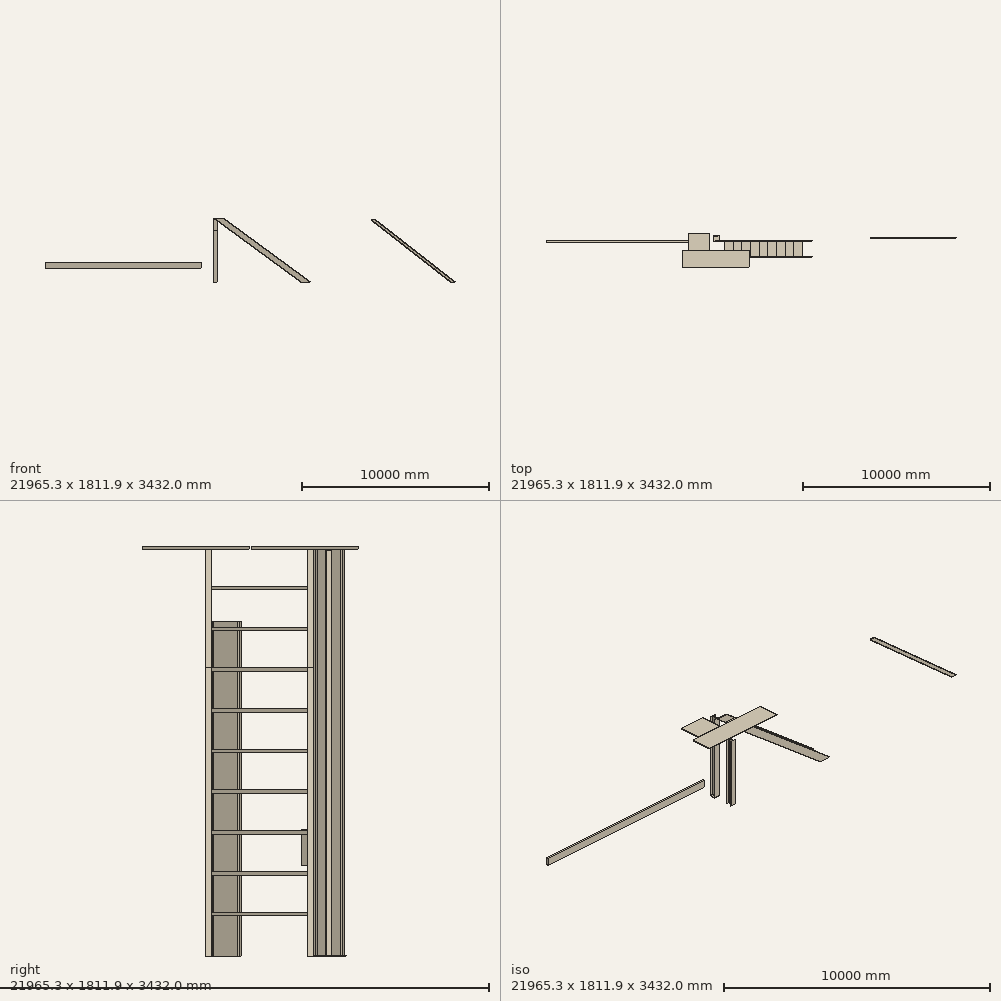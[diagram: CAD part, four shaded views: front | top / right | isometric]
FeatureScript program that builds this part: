
annotation { "Feature Type Name" : "Feature", "Feature Type Description" : "" }
export const myFeature = defineFeature(function(context is Context, id is Id, definition is map)
    precondition{}
    {
        {
            var Q0;
            Q0=qCreatedBy(makeId("Top.planeOp"),FACE);
            var sketch = newSketch(context, id + "F0", { "sketchPlane" : qUnion([Q0])});
            skLineSegment(sketch, "E0.bottom", {"start": v(120, 150) * mm, "end": v(-120, 150) * mm});
            skLineSegment(sketch, "E0.top", {"start": v(120, -150) * mm, "end": v(-120, -150) * mm});
            skLineSegment(sketch, "E0.left", {"start": v(150, 120) * mm, "end": v(150, -120) * mm});
            skLineSegment(sketch, "E0.right", {"start": v(-150, 120) * mm, "end": v(-150, -120) * mm});
            skPoint(sketch, "E0.middle", {"position": v(0, 0) * mm});
            skPoint(sketch, "E1.visualSharp", {"position": v(-150, 150) * mm});
            skArc(sketch, "E1.filletArc", {"start": v(-120, 150) * mm, "mid": v(-141.21, 141.21) * mm, "end": v(-150, 120) * mm});
            skPoint(sketch, "E2.visualSharp", {"position": v(150, 150) * mm});
            skArc(sketch, "E2.filletArc", {"start": v(150, 120) * mm, "mid": v(141.21, 141.21) * mm, "end": v(120, 150) * mm});
            skPoint(sketch, "E3.visualSharp", {"position": v(150, -150) * mm});
            skArc(sketch, "E3.filletArc", {"start": v(120, -150) * mm, "mid": v(141.21, -141.21) * mm, "end": v(150, -120) * mm});
            skPoint(sketch, "E4.visualSharp", {"position": v(-150, -150) * mm});
            skArc(sketch, "E4.filletArc", {"start": v(-150, -120) * mm, "mid": v(-141.21, -141.21) * mm, "end": v(-120, -150) * mm});
            skSolve(sketch);
        }
        {
            var Q0;
            Q0=makeQuery(id+"F0.imprint","IMPRINT",FACE,{"disambiguationData":[TD([[makeQuery(id+"F0.imprint","IMPRINT",EDGE,{"derivedFrom":sQuery(id+"F0.wireOp",EDGE,"E0.bottom")}),1.0]])]});
            extrude(context, id + "F1", {"entities" : qUnion([Q0]), "depth" : 10 * mm, "offsetDistance" : 25 * mm});
        }
        {
            var Q0;
            Q0=makeQuery(id+"F1.opExtrude","CAP_FACE",FACE,{"disambiguationData":[OSD([sQuery(id+"F0.wireOp",EDGE,"E0.bottom"),sQuery(id+"F0.wireOp",EDGE,"E0.top"),sQuery(id+"F0.wireOp",EDGE,"E0.left"),sQuery(id+"F0.wireOp",EDGE,"E0.right"),sQuery(id+"F0.wireOp",EDGE,"E1.filletArc"),sQuery(id+"F0.wireOp",EDGE,"E2.filletArc"),sQuery(id+"F0.wireOp",EDGE,"E3.filletArc"),sQuery(id+"F0.wireOp",EDGE,"E4.filletArc")])],"isStart":false});
            var sketch = newSketch(context, id + "F2", { "sketchPlane" : qUnion([Q0])});
            skLineSegment(sketch, "E5", {"start": v(-128, 130) * mm, "end": v(128, 130) * mm});
            skLineSegment(sketch, "E6", {"start": v(128, 130) * mm, "end": v(128, 112.7) * mm});
            skLineSegment(sketch, "E7", {"start": v(128, 112.7) * mm, "end": v(19.25, 112.7) * mm});
            skArc(sketch, "E8", {"start": v(19.25, 112.7) * mm, "mid": v(9.35, 108.6) * mm, "end": v(5.25, 98.7) * mm});
            skLineSegment(sketch, "E9", {"start": v(5.25, 98.7) * mm, "end": v(5.25, -98.7) * mm});
            skArc(sketch, "E10", {"start": v(5.25, -98.7) * mm, "mid": v(9.35, -108.6) * mm, "end": v(19.25, -112.7) * mm});
            skLineSegment(sketch, "E11", {"start": v(19.25, -112.7) * mm, "end": v(128, -112.7) * mm});
            skLineSegment(sketch, "E12", {"start": v(128, -112.7) * mm, "end": v(128, -130) * mm});
            skLineSegment(sketch, "E13", {"start": v(-128, -130) * mm, "end": v(-128, -112.7) * mm});
            skLineSegment(sketch, "E14", {"start": v(-128, -112.7) * mm, "end": v(-19.25, -112.7) * mm});
            skArc(sketch, "E15", {"start": v(-19.25, -112.7) * mm, "mid": v(-9.35, -108.6) * mm, "end": v(-5.25, -98.7) * mm});
            skLineSegment(sketch, "E16", {"start": v(-5.25, -98.7) * mm, "end": v(-5.25, 98.7) * mm});
            skArc(sketch, "E17", {"start": v(-5.25, 98.7) * mm, "mid": v(-9.35, 108.6) * mm, "end": v(-19.25, 112.7) * mm});
            skLineSegment(sketch, "E18", {"start": v(-19.25, 112.7) * mm, "end": v(-128, 112.7) * mm});
            skLineSegment(sketch, "E19", {"start": v(-128, 112.7) * mm, "end": v(-128, 130) * mm});
            skLineSegment(sketch, "E20", {"start": v(-128, -130) * mm, "end": v(128, -130) * mm});
            skLineSegment(sketch, "E21", {"start": v(5.25, 0) * mm, "end": v(-5.25, 0) * mm});
            skPoint(sketch, "E22", {"position": v(0, 0) * mm});
            skSolve(sketch);
        }
        {
            var Q0;
            Q0=qSketchRegion(id+"F2",true);
            extrude(context, id + "F3", {"entities" : qUnion([Q0]), "operationType" : NewBodyOperationType.ADD, "depth" : 3400 * mm, "offsetDistance" : 25 * mm});
        }
        {
            var Q0;
            Q0=makeQuery(id+"F1.opExtrude","CAP_FACE",FACE,{"disambiguationData":[OSD([sQuery(id+"F0.wireOp",EDGE,"E0.bottom"),sQuery(id+"F0.wireOp",EDGE,"E0.top"),sQuery(id+"F0.wireOp",EDGE,"E0.left"),sQuery(id+"F0.wireOp",EDGE,"E0.right"),sQuery(id+"F0.wireOp",EDGE,"E1.filletArc"),sQuery(id+"F0.wireOp",EDGE,"E2.filletArc"),sQuery(id+"F0.wireOp",EDGE,"E3.filletArc"),sQuery(id+"F0.wireOp",EDGE,"E4.filletArc")])],"isStart":false});
            var sketch = newSketch(context, id + "F4", { "sketchPlane" : qUnion([Q0])});
            skLineSegment(sketch, "E23", {"start": v(125, -75) * mm, "end": v(125, 75) * mm, "construction": true});
            skLineSegment(sketch, "E24", {"start": v(0, 150) * mm, "end": v(0, -150) * mm, "construction": true});
            skCircle(sketch, "E25", {"center": v(125, -75) * mm, "radius": 12.5 * mm});
            skCircle(sketch, "E26", {"center": v(125, 75) * mm, "radius": 12.5 * mm});
            skLineSegment(sketch, "E27", {"start": v(125, 0) * mm, "end": v(150, 0) * mm, "construction": true});
            skCircle(sketch, "E28.MirrorC", {"center": v(-125, -75) * mm, "radius": 12.5 * mm});
            skCircle(sketch, "E29.MirrorC", {"center": v(-125, 75) * mm, "radius": 12.5 * mm});
            skSolve(sketch);
        }
        {
            var Q0;
            Q0=qSketchRegion(id+"F4",true);
            extrude(context, id + "F5", {"entities" : qUnion([Q0]), "operationType" : NewBodyOperationType.REMOVE, "oppositeDirection" : true, "depth" : 25 * mm, "offsetDistance" : 25 * mm});
        }
        {
            var Q0;
            Q0=qCreatedBy(makeId("Top.planeOp"),FACE);
            cPlane(context, id + "F6", {"entities" : qUnion([Q0]), "cplaneType" : CPlaneType.OFFSET, "offset" : 1210 * mm, "width" : 150 * mm, "height" : 150 * mm});
        }
        {
            var Q0;
            Q0=makeQuery(id+"F3.opExtrude","SWEPT_FACE",FACE,{"disambiguationData":[OSD([sQuery(id+"F2.wireOp",EDGE,"E20")])]});
            var sketch = newSketch(context, id + "F7", { "sketchPlane" : qUnion([Q0])});
            skLineSegment(sketch, "E30.bottom", {"start": v(-9105.2, 1063.83) * mm, "end": v(-775.2, 1063.83) * mm});
            skLineSegment(sketch, "E30.top", {"start": v(-9105.2, 763.83) * mm, "end": v(-775.2, 763.83) * mm});
            skLineSegment(sketch, "E30.left", {"start": v(-9105.2, 1063.83) * mm, "end": v(-9105.2, 763.83) * mm});
            skLineSegment(sketch, "E30.right", {"start": v(-775.2, 1063.83) * mm, "end": v(-775.2, 763.83) * mm});
            skSolve(sketch);
        }
        {
            var Q0;
            Q0 = qSketchRegion(id + "F7", true);
            extrude(context, id + "F8", {"entities" : qUnion([Q0]), "depth" : 100 * mm, "offsetDistance" : 25 * mm});
        }
        {
            var Q0;
            Q0=qCreatedBy(makeId("Top.planeOp"),FACE);
            var sketch = newSketch(context, id + "F9", { "sketchPlane" : qUnion([Q0])});
            skLineSegment(sketch, "E31", {"start": v(-128, -733) * mm, "end": v(128, -733) * mm});
            skLineSegment(sketch, "E32", {"start": v(128, -733) * mm, "end": v(128, -750.3) * mm});
            skLineSegment(sketch, "E33", {"start": v(128, -750.3) * mm, "end": v(19.25, -750.3) * mm});
            skArc(sketch, "E34", {"start": v(19.25, -750.3) * mm, "mid": v(9.35, -754.4) * mm, "end": v(5.25, -764.3) * mm});
            skLineSegment(sketch, "E35", {"start": v(5.25, -764.3) * mm, "end": v(5.25, -961.7) * mm});
            skArc(sketch, "E36", {"start": v(5.25, -961.7) * mm, "mid": v(9.35, -971.6) * mm, "end": v(19.25, -975.7) * mm});
            skLineSegment(sketch, "E37", {"start": v(19.25, -975.7) * mm, "end": v(128, -975.7) * mm});
            skLineSegment(sketch, "E38", {"start": v(128, -975.7) * mm, "end": v(128, -993) * mm});
            skLineSegment(sketch, "E39", {"start": v(-128, -993) * mm, "end": v(-128, -975.7) * mm});
            skLineSegment(sketch, "E40", {"start": v(-128, -975.7) * mm, "end": v(-19.25, -975.7) * mm});
            skArc(sketch, "E41", {"start": v(-19.25, -975.7) * mm, "mid": v(-9.35, -971.6) * mm, "end": v(-5.25, -961.7) * mm});
            skLineSegment(sketch, "E42", {"start": v(-5.25, -961.7) * mm, "end": v(-5.25, -764.3) * mm});
            skArc(sketch, "E43", {"start": v(-5.25, -764.3) * mm, "mid": v(-9.35, -754.4) * mm, "end": v(-19.25, -750.3) * mm});
            skLineSegment(sketch, "E44", {"start": v(-19.25, -750.3) * mm, "end": v(-128, -750.3) * mm});
            skLineSegment(sketch, "E45", {"start": v(-128, -750.3) * mm, "end": v(-128, -733) * mm});
            skLineSegment(sketch, "E46", {"start": v(-128, -993) * mm, "end": v(128, -993) * mm});
            skLineSegment(sketch, "E47", {"start": v(5.25, -863) * mm, "end": v(-5.25, -863) * mm});
            skPoint(sketch, "E48", {"position": v(0, -863) * mm});
            skSolve(sketch);
        }
        {
            var Q0;
            Q0 = qSketchRegion(id + "F9", true);
            extrude(context, id + "F10", {"entities" : qUnion([Q0]), "depth" : 2800 * mm, "offsetDistance" : 25 * mm});
        }
        {
            var Q0;
            Q0=makeQuery(id+"F3.opExtrude","CAP_FACE",FACE,{"disambiguationData":[OSD([sQuery(id+"F2.wireOp",EDGE,"E5"),sQuery(id+"F2.wireOp",EDGE,"E6"),sQuery(id+"F2.wireOp",EDGE,"E7"),sQuery(id+"F2.wireOp",EDGE,"E8"),sQuery(id+"F2.wireOp",EDGE,"E9"),sQuery(id+"F2.wireOp",EDGE,"E10"),sQuery(id+"F2.wireOp",EDGE,"E11"),sQuery(id+"F2.wireOp",EDGE,"E12"),sQuery(id+"F2.wireOp",EDGE,"E13"),sQuery(id+"F2.wireOp",EDGE,"E14"),sQuery(id+"F2.wireOp",EDGE,"E15"),sQuery(id+"F2.wireOp",EDGE,"E16"),sQuery(id+"F2.wireOp",EDGE,"E17"),sQuery(id+"F2.wireOp",EDGE,"E18"),sQuery(id+"F2.wireOp",EDGE,"E19"),sQuery(id+"F2.wireOp",EDGE,"E20")])],"isStart":false});
            var sketch = newSketch(context, id + "F11", { "sketchPlane" : qUnion([Q0])});
            skLineSegment(sketch, "E49.bottom", {"start": v(-1838.16, -1561.65) * mm, "end": v(1761.84, -1561.65) * mm});
            skLineSegment(sketch, "E49.top", {"start": v(-1838.16, -661.65) * mm, "end": v(1761.84, -661.65) * mm});
            skLineSegment(sketch, "E49.left", {"start": v(-1838.16, -1561.65) * mm, "end": v(-1838.16, -661.65) * mm});
            skLineSegment(sketch, "E49.right", {"start": v(1761.84, -1561.65) * mm, "end": v(1761.84, -661.65) * mm});
            skSolve(sketch);
        }
        {
            var Q0;
            Q0=makeQuery(id+"F11.imprint","IMPRINT",FACE,{"disambiguationData":[TD([[makeQuery(id+"F11.imprint","IMPRINT",EDGE,{"derivedFrom":sQuery(id+"F11.wireOp",EDGE,"E49.bottom")}),1.0]])]});
            extrude(context, id + "F12", {"entities" : qUnion([Q0]), "depth" : 22 * mm, "offsetDistance" : 25 * mm});
        }
        {
            var Q0;
            Q0=makeQuery(id+"F12.opExtrude","CAP_FACE",FACE,{"disambiguationData":[OSD([sQuery(id+"F11.wireOp",EDGE,"E49.bottom"),sQuery(id+"F11.wireOp",EDGE,"E49.top"),sQuery(id+"F11.wireOp",EDGE,"E49.left"),sQuery(id+"F11.wireOp",EDGE,"E49.right")])],"isStart":false});
            var sketch = newSketch(context, id + "F13", { "sketchPlane" : qUnion([Q0])});
            skLineSegment(sketch, "E50.bottom", {"start": v(-1505.54, 250.28) * mm, "end": v(-375.54, 250.28) * mm});
            skLineSegment(sketch, "E50.top", {"start": v(-1505.54, -649.72) * mm, "end": v(-375.54, -649.72) * mm});
            skLineSegment(sketch, "E50.left", {"start": v(-1505.54, 250.28) * mm, "end": v(-1505.54, -649.72) * mm});
            skLineSegment(sketch, "E50.right", {"start": v(-375.54, 250.28) * mm, "end": v(-375.54, -649.72) * mm});
            skSolve(sketch);
        }
        {
            var Q0;
            Q0=makeQuery(id+"F13.imprint","IMPRINT",FACE,{"disambiguationData":[TD([[makeQuery(id+"F13.imprint","IMPRINT",EDGE,{"derivedFrom":sQuery(id+"F13.wireOp",EDGE,"E50.bottom")}),-1.0]])]});
            extrude(context, id + "F14", {"entities" : qUnion([Q0]), "oppositeDirection" : true, "depth" : 22 * mm, "offsetDistance" : 25 * mm});
        }
        {
            var Q0;
            Q0=makeQuery(id+"F3.opExtrude","SWEPT_FACE",FACE,{"disambiguationData":[OSD([sQuery(id+"F2.wireOp",EDGE,"E20")])]});
            var sketch = newSketch(context, id + "F15", { "sketchPlane" : qUnion([Q0])});
            skLineSegment(sketch, "E51.left", {"start": v(4613.26, 0) * mm, "end": v(4613.26, 341) * mm, "construction": true});
            skLineSegment(sketch, "E52.bottom", {"start": v(4613.26, 341) * mm, "end": v(4148.47, 341) * mm});
            skLineSegment(sketch, "E53.left", {"start": v(4148.47, 341) * mm, "end": v(4148.47, 682) * mm, "construction": true});
            skLineSegment(sketch, "E54.bottom", {"start": v(4148.47, 682) * mm, "end": v(3683.68, 682) * mm});
            skLineSegment(sketch, "E54.left", {"start": v(4148.47, 371) * mm, "end": v(4148.47, 341) * mm, "construction": true});
            skLineSegment(sketch, "E55", {"start": v(3683.68, 682) * mm, "end": v(3683.68, 1023) * mm, "construction": true});
            skLineSegment(sketch, "E56", {"start": v(3683.68, 1023) * mm, "end": v(3218.9, 1023) * mm});
            skLineSegment(sketch, "E57", {"start": v(3218.9, 1023) * mm, "end": v(3218.9, 1364) * mm, "construction": true});
            skLineSegment(sketch, "E58", {"start": v(3218.9, 1364) * mm, "end": v(2754.11, 1364) * mm});
            skLineSegment(sketch, "E59", {"start": v(2754.11, 1364) * mm, "end": v(2754.11, 1705) * mm, "construction": true});
            skLineSegment(sketch, "E60", {"start": v(2754.11, 1705) * mm, "end": v(2289.33, 1705) * mm});
            skLineSegment(sketch, "E61", {"start": v(2289.33, 1705) * mm, "end": v(2289.33, 2046) * mm, "construction": true});
            skLineSegment(sketch, "E62", {"start": v(2289.33, 2046) * mm, "end": v(1824.54, 2046) * mm});
            skLineSegment(sketch, "E63", {"start": v(1824.54, 2046) * mm, "end": v(1824.54, 2387) * mm, "construction": true});
            skLineSegment(sketch, "E64", {"start": v(1824.54, 2387) * mm, "end": v(1359.76, 2387) * mm});
            skLineSegment(sketch, "E65", {"start": v(1359.76, 2387) * mm, "end": v(1359.76, 2728) * mm, "construction": true});
            skLineSegment(sketch, "E66", {"start": v(1359.76, 2728) * mm, "end": v(894.97, 2728) * mm});
            skLineSegment(sketch, "E67", {"start": v(894.97, 2728) * mm, "end": v(894.97, 3069) * mm, "construction": true});
            skLineSegment(sketch, "E68", {"start": v(894.97, 3069) * mm, "end": v(430.18, 3069) * mm});
            skLineSegment(sketch, "E69", {"start": v(430.18, 3069) * mm, "end": v(430.18, 3410) * mm, "construction": true});
            skLineSegment(sketch, "E70", {"start": v(3683.68, 682) * mm, "end": v(3683.68, 652) * mm, "construction": true});
            skLineSegment(sketch, "E71", {"start": v(3683.68, 652) * mm, "end": v(4148.47, 652) * mm, "construction": true});
            skLineSegment(sketch, "E72", {"start": v(3218.9, 1023) * mm, "end": v(3218.9, 993) * mm, "construction": true});
            skLineSegment(sketch, "E73", {"start": v(3218.9, 993) * mm, "end": v(3683.68, 993) * mm, "construction": true});
            skLineSegment(sketch, "E74", {"start": v(2754.11, 1364) * mm, "end": v(2754.11, 1334) * mm, "construction": true});
            skLineSegment(sketch, "E75", {"start": v(2754.11, 1334) * mm, "end": v(3218.9, 1334) * mm, "construction": true});
            skLineSegment(sketch, "E76", {"start": v(2289.33, 1705) * mm, "end": v(2289.33, 1675) * mm, "construction": true});
            skLineSegment(sketch, "E77", {"start": v(2289.33, 1675) * mm, "end": v(2754.11, 1675) * mm, "construction": true});
            skLineSegment(sketch, "E78", {"start": v(1824.54, 2046) * mm, "end": v(1824.54, 2016) * mm, "construction": true});
            skLineSegment(sketch, "E79", {"start": v(1824.54, 2016) * mm, "end": v(2289.33, 2016) * mm, "construction": true});
            skLineSegment(sketch, "E80", {"start": v(1359.76, 2387) * mm, "end": v(1359.76, 2357) * mm, "construction": true});
            skLineSegment(sketch, "E81", {"start": v(1359.76, 2357) * mm, "end": v(1824.54, 2357) * mm, "construction": true});
            skLineSegment(sketch, "E82", {"start": v(894.97, 2728) * mm, "end": v(894.97, 2698) * mm, "construction": true});
            skLineSegment(sketch, "E83", {"start": v(894.97, 2698) * mm, "end": v(1359.76, 2698) * mm, "construction": true});
            skLineSegment(sketch, "E84", {"start": v(430.18, 3069) * mm, "end": v(430.18, 3039) * mm, "construction": true});
            skLineSegment(sketch, "E85", {"start": v(430.18, 3039) * mm, "end": v(894.97, 3039) * mm, "construction": true});
            skLineSegment(sketch, "E86", {"start": v(3683.68, 1023) * mm, "end": v(3683.68, 993) * mm, "construction": true});
            skLineSegment(sketch, "E87", {"start": v(3218.9, 1364) * mm, "end": v(3218.9, 1334) * mm, "construction": true});
            skLineSegment(sketch, "E88", {"start": v(2754.11, 1705) * mm, "end": v(2754.11, 1675) * mm, "construction": true});
            skLineSegment(sketch, "E89", {"start": v(2289.33, 2046) * mm, "end": v(2289.33, 2016) * mm, "construction": true});
            skLineSegment(sketch, "E90", {"start": v(1824.54, 2387) * mm, "end": v(1824.54, 2357) * mm, "construction": true});
            skLineSegment(sketch, "E91", {"start": v(1359.76, 2728) * mm, "end": v(1359.76, 2698) * mm, "construction": true});
            skLineSegment(sketch, "E92", {"start": v(894.97, 3069) * mm, "end": v(894.97, 3039) * mm, "construction": true});
            skLineSegment(sketch, "E93", {"start": v(4613.26, 341) * mm, "end": v(4613.26, 371) * mm});
            skLineSegment(sketch, "E94", {"start": v(4613.26, 371) * mm, "end": v(4148.47, 371) * mm});
            skLineSegment(sketch, "E95", {"start": v(3683.68, 712) * mm, "end": v(3683.68, 682) * mm, "construction": true});
            skLineSegment(sketch, "E96", {"start": v(3218.9, 1023) * mm, "end": v(3218.9, 1053) * mm});
            skLineSegment(sketch, "E97", {"start": v(3218.9, 1053) * mm, "end": v(3683.68, 1053) * mm});
            skLineSegment(sketch, "E98", {"start": v(3683.68, 1053) * mm, "end": v(3683.68, 1023) * mm});
            skLineSegment(sketch, "E99", {"start": v(3218.9, 1364) * mm, "end": v(3218.9, 1394) * mm});
            skLineSegment(sketch, "E100", {"start": v(3218.9, 1394) * mm, "end": v(2754.11, 1394) * mm});
            skLineSegment(sketch, "E101", {"start": v(2754.11, 1394) * mm, "end": v(2754.11, 1364) * mm});
            skLineSegment(sketch, "E102", {"start": v(2754.11, 1705) * mm, "end": v(2754.11, 1735) * mm});
            skLineSegment(sketch, "E103", {"start": v(2754.11, 1735) * mm, "end": v(2289.33, 1735) * mm});
            skLineSegment(sketch, "E104", {"start": v(2289.33, 1735) * mm, "end": v(2289.33, 1705) * mm});
            skLineSegment(sketch, "E105", {"start": v(2289.33, 2046) * mm, "end": v(2289.33, 2076) * mm});
            skLineSegment(sketch, "E106", {"start": v(2289.33, 2076) * mm, "end": v(1824.54, 2076) * mm});
            skLineSegment(sketch, "E107", {"start": v(1824.54, 2076) * mm, "end": v(1824.54, 2046) * mm});
            skLineSegment(sketch, "E108", {"start": v(1824.54, 2387) * mm, "end": v(1824.54, 2420.75) * mm});
            skLineSegment(sketch, "E109", {"start": v(1824.54, 2420.75) * mm, "end": v(1359.76, 2420.75) * mm});
            skLineSegment(sketch, "E110", {"start": v(1359.76, 2420.75) * mm, "end": v(1359.76, 2387) * mm});
            skLineSegment(sketch, "E111", {"start": v(1359.76, 2728) * mm, "end": v(1359.76, 2758) * mm});
            skLineSegment(sketch, "E112", {"start": v(1359.76, 2758) * mm, "end": v(894.97, 2758) * mm});
            skLineSegment(sketch, "E113", {"start": v(894.97, 2758) * mm, "end": v(894.97, 2728) * mm});
            skLineSegment(sketch, "E114", {"start": v(430.18, 3069) * mm, "end": v(430.18, 3099) * mm});
            skLineSegment(sketch, "E115", {"start": v(430.18, 3099) * mm, "end": v(894.97, 3099) * mm});
            skLineSegment(sketch, "E116", {"start": v(894.97, 3099) * mm, "end": v(894.97, 3069) * mm});
            skLineSegment(sketch, "E117", {"start": v(3683.68, 712) * mm, "end": v(4148.47, 712) * mm});
            skLineSegment(sketch, "E118", {"start": v(4148.47, 712) * mm, "end": v(4148.47, 682) * mm});
            skLineSegment(sketch, "E119", {"start": v(3683.68, 712) * mm, "end": v(3683.68, 682) * mm});
            skLineSegment(sketch, "E120", {"start": v(4148.47, 371) * mm, "end": v(4148.47, 341) * mm});
            skSolve(sketch);
        }
        {
            var Q0;
            Q0=makeQuery(id+"F3.opExtrude","SWEPT_FACE",FACE,{"disambiguationData":[OSD([sQuery(id+"F2.wireOp",EDGE,"E20")])]});
            var sketch = newSketch(context, id + "F16", { "sketchPlane" : qUnion([Q0])});
            skLineSegment(sketch, "E121", {"start": v(430.18, 3069) * mm, "end": v(430.18, 0) * mm, "construction": true});
            skLineSegment(sketch, "E122", {"start": v(430.18, 0) * mm, "end": v(5120.4, 0) * mm, "construction": true});
            skLineSegment(sketch, "E123", {"start": v(5120.4, 0) * mm, "end": v(472.55, 3410) * mm});
            skLineSegment(sketch, "E124", {"start": v(430.18, 3069) * mm, "end": v(4613.26, 0) * mm});
            skLineSegment(sketch, "E125", {"start": v(4613.26, 0) * mm, "end": v(5120.4, 0) * mm});
            skLineSegment(sketch, "E126", {"start": v(430.18, 3069) * mm, "end": v(-34.6, 3410) * mm});
            skLineSegment(sketch, "E127", {"start": v(-34.6, 3410) * mm, "end": v(472.55, 3410) * mm});
            skSolve(sketch);
        }
        {
            var Q0;
            Q0=makeQuery(id+"F16.imprint","IMPRINT",FACE,{"disambiguationData":[TD([[makeQuery(id+"F16.imprint","IMPRINT",EDGE,{"derivedFrom":sQuery(id+"F16.wireOp",EDGE,"E123")}),1.0]])]});
            var Q1;
            {var subQ0=sQuery(id+"F16.wireOp",EDGE,"E127");var subQ1=sQuery(id+"F16.wireOp",EDGE,"E126");var subQ2=sQuery(id+"F2.wireOp",EDGE,"E20");var subQ3=makeQuery(id+"F16.imprint","INTERSECT",VERTEX,{"derivedFrom":[makeQuery(id+"F3.opExtrude","CAP_EDGE",EDGE,{"disambiguationData":[OSD([subQ2])],"isStart":false}),subQ1,subQ0]});Q1=makeQuery(id+"F16.imprint","IMPRINT",FACE,{"disambiguationData":[TD([[makeQuery(id+"F16.imprint","IMPRINT",EDGE,{"disambiguationData":[TD([[subQ3,1.0]])],"derivedFrom":subQ1}),-1.0]])]});}
            extrude(context, id + "F17", {"entities" : qUnion([Q0, Q1]), "depth" : 50 * mm, "offsetDistance" : 25 * mm});
        }
        {
            var Q0;
            Q0 = qSketchRegion(id + "F15", true);
            extrude(context, id + "F18", {"entities" : qUnion([Q0]), "operationType" : NewBodyOperationType.ADD, "depth" : 900 * mm, "offsetDistance" : 25 * mm});
        }
        {
            var Q0;
            Q0 = qSketchRegion(id + "F16", true);
            extrude(context, id + "F19", {"entities" : qUnion([Q0]), "operationType" : NewBodyOperationType.ADD, "depth" : 900 * mm, "hasOffset" : true, "offsetDistance" : 1000 * mm, "hasSecondDirection" : true, "secondDirectionOppositeDirection" : false, "secondDirectionDepth" : 850 * mm});
        }
        {
            var Q0;
            Q0=qCreatedBy(makeId("Front.planeOp"),FACE);
            var sketch = newSketch(context, id + "F20", { "sketchPlane" : qUnion([Q0])});
            skLineSegment(sketch, "E128", {"start": v(156.1, 0) * mm, "end": v(14567.44, 0) * mm, "construction": true});
            skLineSegment(sketch, "E129", {"start": v(14567.44, 0) * mm, "end": v(14567.44, 3410) * mm, "construction": true});
            skLineSegment(sketch, "E130", {"start": v(-129.2, 3410) * mm, "end": v(14567.44, 3410) * mm, "construction": true});
            skLineSegment(sketch, "E131", {"start": v(8386.5, 3410) * mm, "end": v(12751.1, 0) * mm, "construction": true});
            skSolve(sketch);
        }
        {
            var Q0;
            Q0=sQuery(id+"F20.wireOp",EDGE,"E131");
            var Q1;
            Q1=sQuery(id+"F20.wireOp",VERTEX,"E131.end");
            cPlane(context, id + "F21", {"entities" : qUnion([Q0, Q1]), "cplaneType" : CPlaneType.LINE_POINT, "offset" : 25 * mm, "width" : 150 * mm, "height" : 150 * mm});
        }
        {
            var Q0;
            Q0=qCreatedBy(id+"F21.planeOp",FACE);
            var sketch = newSketch(context, id + "F22", { "sketchPlane" : qUnion([Q0])});
            skLineSegment(sketch, "E132.bottom", {"start": v(-20, 7925.36) * mm, "end": v(20, 7925.36) * mm});
            skLineSegment(sketch, "E132.top", {"start": v(-20, 7775.36) * mm, "end": v(20, 7775.36) * mm});
            skLineSegment(sketch, "E132.left", {"start": v(-25, 7920.36) * mm, "end": v(-25, 7780.36) * mm});
            skLineSegment(sketch, "E132.right", {"start": v(25, 7920.36) * mm, "end": v(25, 7780.36) * mm});
            skPoint(sketch, "E132.middle", {"position": v(0, 7850.36) * mm});
            skLineSegment(sketch, "E133.0", {"start": v(22.5, 7917.86) * mm, "end": v(22.5, 7782.86) * mm});
            skLineSegment(sketch, "E133.1", {"start": v(-17.5, 7922.86) * mm, "end": v(17.5, 7922.86) * mm});
            skLineSegment(sketch, "E133.2", {"start": v(-22.5, 7917.86) * mm, "end": v(-22.5, 7782.86) * mm});
            skLineSegment(sketch, "E133.3", {"start": v(-17.5, 7777.86) * mm, "end": v(17.5, 7777.86) * mm});
            skPoint(sketch, "E134.visualSharp", {"position": v(22.5, 7777.86) * mm});
            skArc(sketch, "E134.filletArc", {"start": v(17.5, 7777.86) * mm, "mid": v(21.04, 7779.32) * mm, "end": v(22.5, 7782.86) * mm});
            skPoint(sketch, "E135.visualSharp", {"position": v(25, 7775.36) * mm});
            skArc(sketch, "E135.filletArc", {"start": v(20, 7775.36) * mm, "mid": v(23.54, 7776.82) * mm, "end": v(25, 7780.36) * mm});
            skPoint(sketch, "E136.visualSharp", {"position": v(25, 7925.36) * mm});
            skArc(sketch, "E136.filletArc", {"start": v(25, 7920.36) * mm, "mid": v(23.54, 7923.9) * mm, "end": v(20, 7925.36) * mm});
            skPoint(sketch, "E137.visualSharp", {"position": v(22.5, 7922.86) * mm});
            skArc(sketch, "E137.filletArc", {"start": v(22.5, 7917.86) * mm, "mid": v(21.04, 7921.4) * mm, "end": v(17.5, 7922.86) * mm});
            skPoint(sketch, "E138.visualSharp", {"position": v(-22.5, 7922.86) * mm});
            skArc(sketch, "E138.filletArc", {"start": v(-17.5, 7922.86) * mm, "mid": v(-21.04, 7921.4) * mm, "end": v(-22.5, 7917.86) * mm});
            skPoint(sketch, "E139.visualSharp", {"position": v(-25, 7925.36) * mm});
            skArc(sketch, "E139.filletArc", {"start": v(-20, 7925.36) * mm, "mid": v(-23.54, 7923.9) * mm, "end": v(-25, 7920.36) * mm});
            skPoint(sketch, "E140.visualSharp", {"position": v(-22.5, 7777.86) * mm});
            skArc(sketch, "E140.filletArc", {"start": v(-22.5, 7782.86) * mm, "mid": v(-21.04, 7779.32) * mm, "end": v(-17.5, 7777.86) * mm});
            skPoint(sketch, "E141.visualSharp", {"position": v(-25, 7775.36) * mm});
            skArc(sketch, "E141.filletArc", {"start": v(-25, 7780.36) * mm, "mid": v(-23.54, 7776.82) * mm, "end": v(-20, 7775.36) * mm});
            skSolve(sketch);
        }
        {
            var Q0;
            Q0 = qSketchRegion(id + "F22", true);
            var Q1;
            Q1=sQuery(id+"F20.wireOp",VERTEX,"E131.start");
            extrude(context, id + "F23", {"entities" : qUnion([Q0]), "oppositeDirection" : true, "depth" : 5740 * mm, "endBoundEntityVertex" : qUnion([Q1]), "offsetDistance" : 25 * mm});
        }
        {
            var Q0;
            Q0 = qSketchRegion(id + "F22", true);
            extrude(context, id + "F24", {"entities" : qUnion([Q0]), "operationType" : NewBodyOperationType.ADD, "depth" : 100 * mm, "offsetDistance" : 25 * mm});
        }
        {
            var Q0;
            Q0=qCreatedBy(makeId("Front.planeOp"),FACE);
            var sketch = newSketch(context, id + "F25", { "sketchPlane" : qUnion([Q0])});
            skLineSegment(sketch, "E142.bottom", {"start": v(12926.42, 10) * mm, "end": v(12577.42, 10) * mm});
            skLineSegment(sketch, "E142.top", {"start": v(12926.42, -126.31) * mm, "end": v(12577.42, -126.31) * mm});
            skLineSegment(sketch, "E142.left", {"start": v(12926.42, 10) * mm, "end": v(12926.42, -126.31) * mm});
            skLineSegment(sketch, "E142.right", {"start": v(12577.42, 10) * mm, "end": v(12577.42, -126.31) * mm});
            skLineSegment(sketch, "E143.bottom", {"start": v(8027.27, 3700.34) * mm, "end": v(8650.93, 3700.34) * mm});
            skLineSegment(sketch, "E143.top", {"start": v(8027.27, 3400) * mm, "end": v(8650.93, 3400) * mm});
            skLineSegment(sketch, "E143.left", {"start": v(8027.27, 3700.34) * mm, "end": v(8027.27, 3400) * mm});
            skLineSegment(sketch, "E143.right", {"start": v(8650.93, 3700.34) * mm, "end": v(8650.93, 3400) * mm});
            skSolve(sketch);
        }
        {
            var Q0;
            Q0=makeQuery(id+"F25.imprint","IMPRINT",FACE,{"disambiguationData":[TD([[makeQuery(id+"F25.imprint","IMPRINT",EDGE,{"derivedFrom":sQuery(id+"F25.wireOp",EDGE,"E143.bottom")}),-1.0]])]});
            var Q1;
            Q1=makeQuery(id+"F25.imprint","IMPRINT",FACE,{"disambiguationData":[TD([[makeQuery(id+"F25.imprint","IMPRINT",EDGE,{"derivedFrom":sQuery(id+"F25.wireOp",EDGE,"E142.bottom")}),1.0]])]});
            extrude(context, id + "F26", {"entities" : qUnion([Q0, Q1]), "operationType" : NewBodyOperationType.REMOVE, "endBound" : BoundingType.SYMMETRIC, "oppositeDirection" : true, "depth" : 200 * mm, "offsetDistance" : 25 * mm});
        }
    });
